# Revit family: Hager-IC-IP30-syst-NoHosted-PL-pl
name_source: partatom
category: Electrical Equipment
units: mm (PartAtom-declared; Revit-internal decimal feet)

## family parameters
Always vertical = Yes
Cut with Voids When Loaded = No
Panel Configuration = Two Columns, Circuits Across
Part Type = Panelboard
Room Calculation Point = No
Round Connector Dimension = Use Diameter
Shared = No
Work Plane-Based = Yes

## types (14) — shared parameters
Default Elevation = 1219 mm
EF000007 - Kolor = EV000202 - Biały
EF000116 - Numer RAL = 9010
EF000118 - Z płytą montażową = No
EF001062 - Wykonane zgodnie z Dyrektywą Kompatybilności Elektromagnetycznej EMC = No
EF001088 - Możliwość rozbudowy = Yes
EF001131 - Głębokość wewnętrzna = 72 mm  [stored 0.23622 ft]
EF001134 - Szyna DIN = Yes
EF001596 - Materiał obudowy = EV000139 - Tworzywo sztuczne
EF004462 - Rodzaj zamknięcia = EV000154 - Inne
EF005474 - Stopień ochrony (IP) = EV006410 - IP30
EF006244 - Transparentna pokrywa/drzwi = No
EF006306 - Z zamkiem = No
EF009212 - Wykonanie pokrywy = EV000116 - Zamknięty
EF015941 - Drzwi przepuszczające sygnał = Yes
HG000001 - Liczba kolumn = 1
HG000002 - Z drzwiami lub pokrywą = No
HG000003 - Zakres = IC
HG000005 - Grubość = 3 mm  [stored 0.00984252 ft]
HG000009 - Drzwi dwuskrzydłowe = No
HG000010 - Drzwi asymetryczne = No
HG000011 - Puste rzędy od dołu = No
HG000017 - Odległość między biegunami = 18 mm  [stored 0.0590551 ft]
Manufacturer = Hager
Type Comments = IC
zero-valued in all types: HG000007 - Liczba pustych kolumn, HG000008 - Liczba pustych rzędów

## per-type parameters (varying)
| type | EF000003 - Sposób montażu | EF000008 - Szerokość | EF000040 - Wysokość | EF000049 - Głębokość | EF000218 - Głębokość wbudowania | EF000266 - Liczba rzędów | EF000332 - Wysokość wbudowania | EF000846 - Szerokość wbudowania | EF002950 - Szerokość wyrażona liczbą modułów | EF015776 - Listwa zaciskowa uziemienia | EF015777 - Listwa zaciskowa przewodu neutralnego | HG000004 - Referencja producenta | HG000006 - Montaż podtynkowy | Model |
| Montaż natynkowy IP30 S134.5 W170 G91 6 Jednostki dywizyjne - VD106NP | EV000384 - Montaż natynkowy | 134 mm | 170 mm  [stored 0.557743 ft] | 91 mm  [stored 0.298556 ft] | 0 mm  [stored 0 ft] | 1 | 0 mm  [stored 0 ft] | 0 mm  [stored 0 ft] | 6 | Yes | Yes | VD106NP | No | VD106NP |
| Montaż natynkowy IP30 S170.5 W170 G91 8 Jednostki dywizyjne - VD108NP | EV000384 - Montaż natynkowy | 170 mm  [stored 0.557743 ft] | 170 mm  [stored 0.557743 ft] | 91 mm  [stored 0.298556 ft] | 0 mm  [stored 0 ft] | 1 | 0 mm  [stored 0 ft] | 0 mm  [stored 0 ft] | 8 | Yes | Yes | VD108NP | No | VD108NP |
| Montaż natynkowy IP30 S206.5 W170 G91 10 Jednostki dywizyjne - VD110NP | EV000384 - Montaż natynkowy | 206 mm  [stored 0.675853 ft] | 170 mm  [stored 0.557743 ft] | 91 mm  [stored 0.298556 ft] | 0 mm  [stored 0 ft] | 1 | 0 mm  [stored 0 ft] | 0 mm  [stored 0 ft] | 10 | Yes | Yes | VD110NP | No | VD110NP |
| Montaż natynkowy IP30 S27.5 W163.5 G71 1 Jednostki dywizyjne - VD101NE | EV000384 - Montaż natynkowy | 28 mm  [stored 0.0918635 ft] | 164 mm  [stored 0.538058 ft] | 71 mm  [stored 0.23294 ft] | 0 mm  [stored 0 ft] | 1 | 0 mm  [stored 0 ft] | 0 mm  [stored 0 ft] | 1 | No | No | VD101NE | No | VD101NE |
| Montaż natynkowy IP30 S292.5 W200 G91 12 Jednostki dywizyjne - VD112NP | EV000384 - Montaż natynkowy | 292 mm  [stored 0.958005 ft] | 200 mm  [stored 0.656168 ft] | 91 mm  [stored 0.298556 ft] | 0 mm  [stored 0 ft] | 1 | 0 mm  [stored 0 ft] | 0 mm  [stored 0 ft] | 12 | Yes | Yes | VD112NP | No | VD112NP |
| Montaż natynkowy IP30 S294 W326.5 G92.5 12 Jednostki dywizyjne - VD212NP | EV000384 - Montaż natynkowy | 294 mm  [stored 0.964567 ft] | 326 mm  [stored 1.06955 ft] | 92 mm  [stored 0.301837 ft] | 0 mm  [stored 0 ft] | 2 | 0 mm  [stored 0 ft] | 0 mm  [stored 0 ft] | 12 | Yes | Yes | VD212NP | No | VD212NP |
| Montaż natynkowy IP30 S400 W200 G91 18 Jednostki dywizyjne - VD118NP | EV000384 - Montaż natynkowy | 400 mm  [stored 1.31234 ft] | 200 mm  [stored 0.656168 ft] | 91 mm  [stored 0.298556 ft] | 0 mm  [stored 0 ft] | 1 | 0 mm  [stored 0 ft] | 0 mm  [stored 0 ft] | 18 | Yes | Yes | VD118NP | No | VD118NP |
| Montaż natynkowy IP30 S45.5 W163.5 G71 2 Jednostki dywizyjne - VD102NE | EV000384 - Montaż natynkowy | 46 mm  [stored 0.150919 ft] | 164 mm  [stored 0.538058 ft] | 71 mm  [stored 0.23294 ft] | 0 mm  [stored 0 ft] | 1 | 0 mm  [stored 0 ft] | 0 mm  [stored 0 ft] | 2 | No | No | VD102NE | No | VD102NE |
| Montaż natynkowy IP30 S63.5 W163.5 G71 3 Jednostki dywizyjne - VD103NE | EV000384 - Montaż natynkowy | 64 mm  [stored 0.209974 ft] | 164 mm  [stored 0.538058 ft] | 71 mm  [stored 0.23294 ft] | 0 mm  [stored 0 ft] | 1 | 0 mm  [stored 0 ft] | 0 mm  [stored 0 ft] | 3 | No | No | VD103NE | No | VD103NE |
| Montaż natynkowy IP30 S81.5 W163.5 G71 4 Jednostki dywizyjne - VD104NE | EV000384 - Montaż natynkowy | 82 mm  [stored 0.269029 ft] | 164 mm  [stored 0.538058 ft] | 71 mm  [stored 0.23294 ft] | 0 mm  [stored 0 ft] | 1 | 0 mm  [stored 0 ft] | 0 mm  [stored 0 ft] | 4 | No | No | VD104NE | No | VD104NE |
| Montaż podtynkowy IP30 S236 W206 G91.4 8 Jednostki dywizyjne - VR108NP | EV000383 - Montaż podtynkowy | 236 mm | 206 mm  [stored 0.675853 ft] | 91 mm  [stored 0.298556 ft] | 72 mm  [stored 0.23622 ft] | 1 | 188 mm  [stored 0.616798 ft] | 218 mm  [stored 0.715223 ft] | 8 | Yes | Yes | VR108NP | Yes | VR108NP |
| Montaż podtynkowy IP30 S308 W226 G91.4 12 Jednostki dywizyjne - VR112NP | EV000383 - Montaż podtynkowy | 308 mm  [stored 1.0105 ft] | 226 mm  [stored 0.74147 ft] | 91 mm  [stored 0.298556 ft] | 72 mm  [stored 0.23622 ft] | 1 | 208 mm | 290 mm  [stored 0.951444 ft] | 12 | Yes | Yes | VR112NP | Yes | VR112NP |
| Montaż podtynkowy IP30 S308 W351 G93 12 Jednostki dywizyjne - VR212NP | EV000383 - Montaż podtynkowy | 308 mm  [stored 1.0105 ft] | 351 mm  [stored 1.15157 ft] | 93 mm  [stored 0.305118 ft] | 72 mm  [stored 0.23622 ft] | 2 | 333 mm  [stored 1.09252 ft] | 290 mm  [stored 0.951444 ft] | 12 | Yes | Yes | VR212NP | Yes | VR212NP |
| Montaż podtynkowy IP30 S416 W226 G91.4 18 Jednostki dywizyjne - VR118NP | EV000383 - Montaż podtynkowy | 416 mm | 226 mm  [stored 0.74147 ft] | 91 mm  [stored 0.298556 ft] | 72 mm  [stored 0.23622 ft] | 1 | 208 mm | 398 mm  [stored 1.30577 ft] | 18 | Yes | Yes | VR118NP | Yes | VR118NP |

note: [stored X ft] marks values corroborated as IEEE doubles in the binary element streams (Revit-internal decimal feet)

## geometry (parser evidence)
native form markers: Sweep x13
no freeform markers — native parametric forms only
